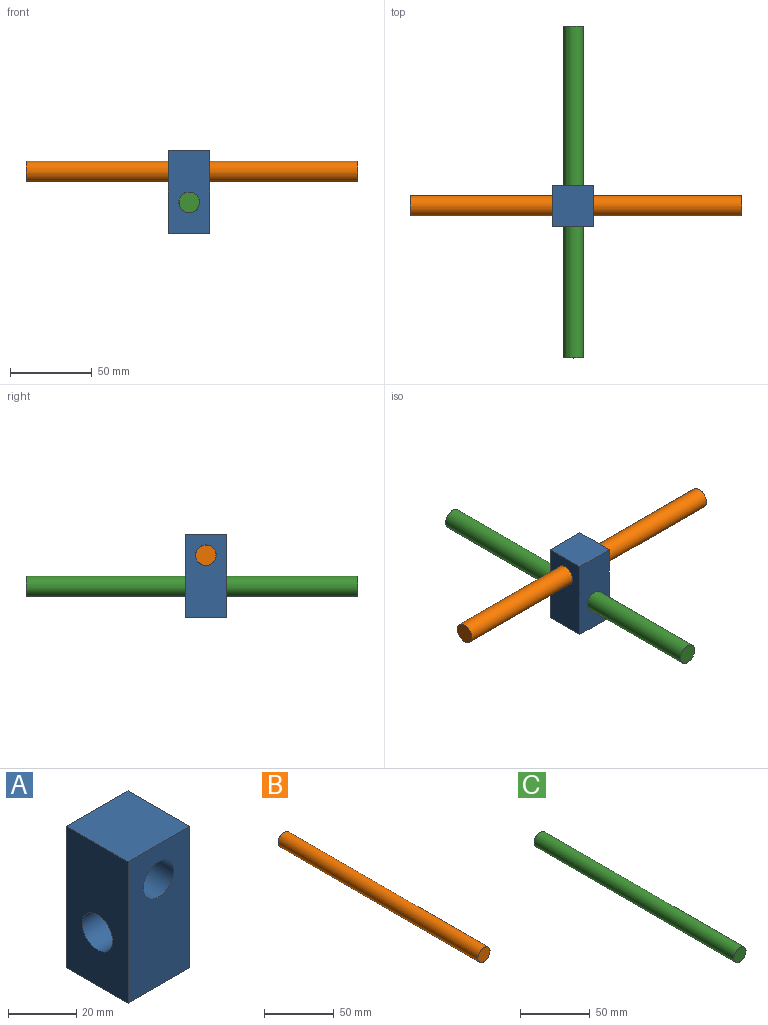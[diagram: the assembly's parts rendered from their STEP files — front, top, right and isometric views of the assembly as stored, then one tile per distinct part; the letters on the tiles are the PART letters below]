
ASSEMBLY  parts=3 mates=2
PART A: 8 faces, bbox 25.4x25.4x50.8 mm
  f0: plane 50.8x25.4mm, normal (-1,0,0), area 1163.6mm2, adj f1,f3,f5,f6,f7
  f1: plane 25.4x25.4mm, normal (0,0,-1), area 645.2mm2, adj f0,f2,f5,f6
  f2: plane 50.8x25.4mm, normal (1,0,0), area 1163.6mm2, adj f1,f3,f5,f6,f7
  f3: plane 25.4x25.4mm, normal (0,0,1), area 645.2mm2, adj f0,f2,f5,f6
  f4: cylinder r=6.35mm len=25.4mm, axis (0,1,0), area 1013.4mm2, adj f5,f6
  f5: plane 50.8x25.4mm, normal (0,-1,0), area 1163.6mm2, adj f0,f1,f2,f3,f4
  f6: plane 50.8x25.4mm, normal (0,1,0), area 1163.6mm2, adj f0,f1,f2,f3,f4
  f7: cylinder r=6.35mm len=25.4mm, axis (1,0,0), area 1013.4mm2, adj f0,f2
PART B: 3 faces, bbox 12.4x203.2x12.4 mm
  f0: cylinder r=6.22mm len=203.2mm, axis (0,-1,0), area 7945.2mm2, adj f1,f2
  f1: plane 12.45x12.45mm, normal (0,1,0), area 121.7mm2, adj f0
  f2: plane 12.45x12.45mm, normal (0,-1,0), area 121.7mm2, adj f0
PART C: 3 faces, bbox 12.4x203.2x12.4 mm
  f0: cylinder r=6.22mm len=203.2mm, axis (0,-1,0), area 7945.2mm2, adj f1,f2
  f1: plane 12.45x12.45mm, normal (0,1,0), area 121.7mm2, adj f0
  f2: plane 12.45x12.45mm, normal (0,-1,0), area 121.7mm2, adj f0
PLACE A rot(axis=(0,0,-1),90deg) t=(9.44,-11.27,82.58)mm
PLACE B rot(axis=(-0.67,0.67,0.32),144deg) t=(100.05,-64.55,50.18)mm
PLACE C rot(axis=(0,-1,0),23.7deg) t=(-58.05,-104.39,105.55)mm
MATE cylindrical A.f4 <-> B.f0  axis (1,0,0) through (9.44,-11.27,95.28)mm
MATE cylindrical C.f0 <-> A.f7  axis (0,-1,0) through (-3.26,-2.79,76.23)mm
